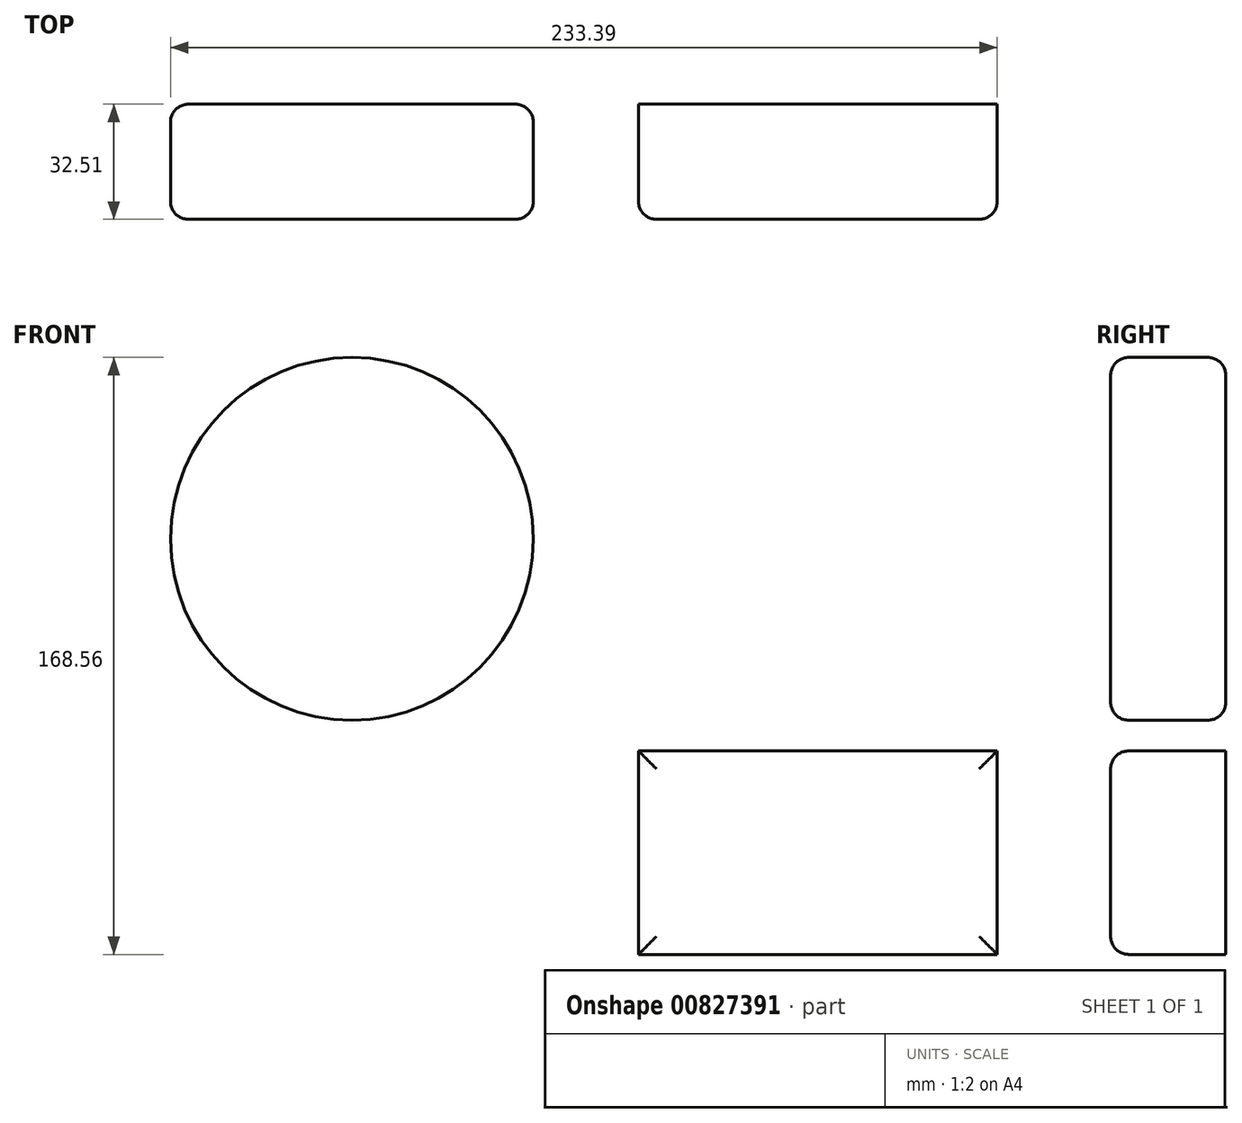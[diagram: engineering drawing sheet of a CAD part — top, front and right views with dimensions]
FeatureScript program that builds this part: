
annotation { "Feature Type Name" : "Feature", "Feature Type Description" : "" }
export const myFeature = defineFeature(function(context is Context, id is Id, definition is map)
    precondition{}
    {
        {
            var Q0;
            Q0=qCreatedBy(makeId("Front.planeOp"),FACE);
            var sketch = newSketch(context, id + "F0", { "sketchPlane" : qUnion([Q0])});
            skCircle(sketch, "E0", {"center": v(-35.78, 37.46) * mm, "radius": 51.21 * mm});
            skLineSegment(sketch, "E1.bottom", {"start": v(45.1, -22.42) * mm, "end": v(146.4, -22.42) * mm});
            skLineSegment(sketch, "E1.top", {"start": v(45.1, -79.9) * mm, "end": v(146.4, -79.9) * mm});
            skLineSegment(sketch, "E1.left", {"start": v(45.1, -22.42) * mm, "end": v(45.1, -79.9) * mm});
            skLineSegment(sketch, "E1.right", {"start": v(146.4, -22.42) * mm, "end": v(146.4, -79.9) * mm});
            skSolve(sketch);
        }
        {
            var Q0;
            Q0=makeQuery(id+"F0.imprint","IMPRINT",FACE,{"disambiguationData":[TD([[makeQuery(id+"F0.imprint","IMPRINT",EDGE,{"derivedFrom":sQuery(id+"F0.wireOp",EDGE,"E0")}),1.0]])]});
            var Q1;
            Q1=makeQuery(id+"F0.imprint","IMPRINT",FACE,{"disambiguationData":[TD([[makeQuery(id+"F0.imprint","IMPRINT",EDGE,{"derivedFrom":sQuery(id+"F0.wireOp",EDGE,"E1.bottom")}),-1.0]])]});
            extrude(context, id + "F1", {"entities" : qUnion([Q0, Q1]), "oppositeDirection" : true, "depth" : 32.5 * mm, "offsetDistance" : 25.4 * mm});
        }
        {
            var Q0;
            Q0=makeQuery(id+"F1.opExtrude","SWEPT_FACE",FACE,{"disambiguationData":[OSD([sQuery(id+"F0.wireOp",EDGE,"E0")])]});
            var Q1;
            Q1=makeQuery(id+"F1.opExtrude","CAP_EDGE",EDGE,{"disambiguationData":[OSD([sQuery(id+"F0.wireOp",EDGE,"E0")])],"isStart":true});
            var Q2;
            Q2=makeQuery(id+"F1.opExtrude","CAP_FACE",FACE,{"disambiguationData":[OSD([sQuery(id+"F0.wireOp",EDGE,"E1.bottom"),sQuery(id+"F0.wireOp",EDGE,"E1.top"),sQuery(id+"F0.wireOp",EDGE,"E1.left"),sQuery(id+"F0.wireOp",EDGE,"E1.right")])],"isStart":true});
            fillet(context, id + "F2", {"entities" : qUnion([Q0, Q1, Q2]), "radius" : 5.08 * mm, "tangentPropagation" : true, "allowEdgeOverflow" : false});
        }
    });
